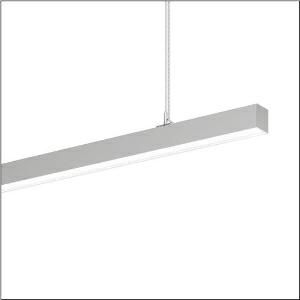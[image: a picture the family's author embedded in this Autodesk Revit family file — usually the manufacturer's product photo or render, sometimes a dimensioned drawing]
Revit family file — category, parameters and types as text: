
# Revit family: silica_r__21_51mx30tat4s_875d
name_source: partatom
category: Lighting Fixtures
units: mm (PartAtom-declared; Revit-internal decimal feet)

## family parameters
Cut with Voids When Loaded = No
Host = Face
Light Source = No
Part Type = Normal
Room Calculation Point = No
Round Connector Dimension = Use Diameter
Shared = No

## types (1)
- --- (1 x LED, 4120 lm, 33.8 W, 6500K)
    Apparent Load = 34 VA
    CIE Flux Codes = 47 79 96 58 100
    Color Rendering = 80
    Color Temperature = 6500K
    Default Elevation = 1800 mm
    Description = Silica® 21, office luminaire, primary optical cover: cover, of PMMA, opal, light emission: direct/indirect distribution, primary light characteristic: symmetric, installation type: suspended mounting, LED, rated luminous flux: 4.120lm, luminous efficacy: 116lm/W, light colour: 8tw, colour temperature: 2700..6500K, control gear: ECG DALI, with terminal, 3+2-pole, max. 2.5mm², mains connection: 220..240V, AC, 50/60Hz, rated input power: 35.5W, luminaire housing, of aluminium, metallic grey (RAL 9006), length: 1.204mm, width: 53mm, height: 53mm, protection rating (complete): IP20, insulation class (complete): insulation class I (protective earthing), certification: CE, permissible operating ambient temperature: 0..+35°C, standard: EN 50419, packaging unit: 1 piece
    Height = 53 mm
    Lamp = 1 x LED
    Lamp Light Flux = 4120 lm
    Lamp Power = 33.8 W
    Lamp count = 1
    Length = 1204 mm
    Luminous efficacy = 122 lm/W
    Manufacturer = Siteco
    ModVariant = No
    Model = 51MX30TAT4S
    Mounting Place = Ceiling
    Mounting Type = Pendant
    Number of Poles = 1
    OnlyDefault = Yes
    Power Factor = 1
    Product Name = Silica® 21
    Product group = office luminaire | ceiling pendant
    ProductGroupID = 902
    Protection Class = Protection class I
    Protection Degree = IP 20
    RLX_Detail_Level = 1
    RLX_Emergency_Light_Flux = 0 lm
    RLX_Emergency_Type = 0
    RLX_Emergency_Type_DB = No
    RlxData = <blob elided: 20125 chars, md5=f39935fe>
    Socket = socket
    Standby Power = 0 W
    System Light Flux = 4120 lm
    System Power = 34 W
    Type Comments = individual setting
    Type Image = l_1313621.jpg
    URL = http://relux.com
    VarID = @adj_088989
    Voltage = 0 V
    Weight = 0.00 kg
    Width = 53 mm

## geometry (parser evidence)
native form markers: Blend x4, Sweep x14
no freeform markers — native parametric forms only
